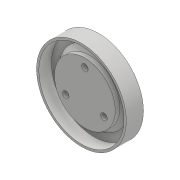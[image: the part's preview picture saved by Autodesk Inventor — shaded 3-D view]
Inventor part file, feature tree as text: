
AUTODESK INVENTOR PART (.ipt)
format: ipt  version: 2017 (Build 210142000, 142)  size: 138,240 bytes
history: native  units: mm
features: sketch x5, extrude x4, hole x1, chamfer x1
ambient origin geometry x8: Origin, YZ Plane, XZ Plane, XY Plane, X Axis, Y Axis, Z Axis, Center Point
bodies: Solid1 (feature_tree)
feature tree (11):
  extrude  "Extrusion1"  Depth=6.0mm TaperAngle=0.0deg
  extrude  "Extrusion2"  Depth=3.0mm TaperAngle=0.0deg
  extrude  "Extrusion3"  Depth=8.3mm TaperAngle=0.0deg
  hole  "Hole1"  [1 undecoded]
  chamfer  "Chamfer1"  Distance=3.0mm Angle=45.0deg
  extrude  "Extrusion4"  Depth=5.0mm
  sketch  "Sketch1"  dims[d0=40.0mm d1=6.0mm d2=0.0mm]
  sketch  "Sketch2"  dims[d3=59.0mm d4=3.0mm d5=0.0mm]
  sketch  "Sketch3"  dims[d6=56.0mm d7=8.3mm d8=0.0mm]
  sketch  "Sketch4"  dims[d9=29.0mm d10=30.0mm d12=360.0deg]
  sketch  "Sketch5"  dims[d14=4.3mm d15=6.0mm d16=4.0mm d17=2.0mm d18=90.0deg d19=8.0mm d20=20.594885mm d21=3.0mm d22=2.0mm d23=45.0deg d24=8.5mm d25=8.5mm d26=8.5mm d27=5.0mm d28=0.0mm]
note: 1 required parameter value undecoded (feature->parameter linkage not recoverable at this tier; creation-order binding heuristic only, values carry confidence <= 0.55)
